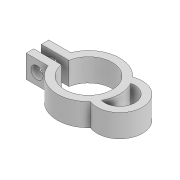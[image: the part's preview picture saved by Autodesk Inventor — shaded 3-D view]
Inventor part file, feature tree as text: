
AUTODESK INVENTOR PART (.ipt)
format: ipt  version: 2022 (Build 260153000, 153)  size: 124,928 bytes
history: native  units: mm
features: extrude x2, sketch x2, projected_geometry x1
ambient origin geometry x8: Origin, YZ Plane, XZ Plane, XY Plane, X Axis, Y Axis, Z Axis, Center Point
bodies: Solid1 (feature_tree)
feature tree (5):
  extrude  "Extrusion1"  Depth=2.0mm
  extrude  "Extrusion2"  Depth=2.0mm
  sketch  "Sketch1"  dims[d0=12.5mm d1=2.0mm]
  sketch  "Sketch2"  dims[d2=2.0mm d3=2.0mm d4=1.0mm d5=1.0mm d6=8.0mm d7=8.0mm d8=8.0mm d9=2.0mm d10=6.0mm d11=0.0mm d12=3.2mm d13=10.0mm d14=0.0mm]
  projected_geometry  "Projected Loop1"
